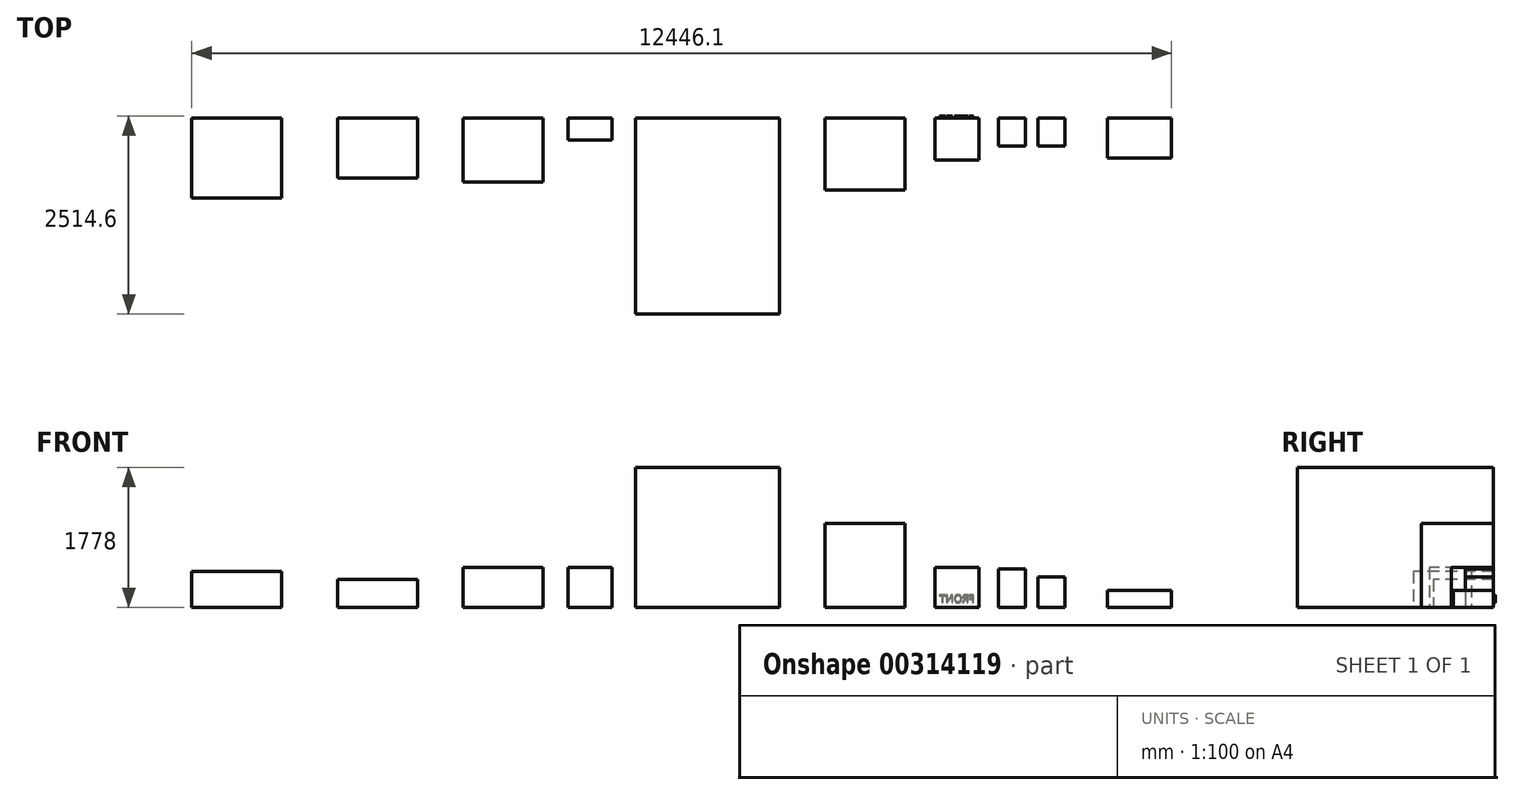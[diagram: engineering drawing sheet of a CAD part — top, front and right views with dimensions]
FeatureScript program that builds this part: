
annotation { "Feature Type Name" : "Feature", "Feature Type Description" : "" }
export const myFeature = defineFeature(function(context is Context, id is Id, definition is map)
    precondition{}
    {
        {
            var Q0;
            Q0=qCreatedBy(makeId("Top.planeOp"),FACE);
            var sketch = newSketch(context, id + "F0", { "sketchPlane" : qUnion([Q0])});
            skLineSegment(sketch, "E0.bottom", {"start": v(-6803, -5124.32) * mm, "end": v(-5660, -5124.32) * mm});
            skLineSegment(sketch, "E0.top", {"start": v(-6803, -6140.32) * mm, "end": v(-5660, -6140.32) * mm});
            skLineSegment(sketch, "E0.left", {"start": v(-6803, -5124.32) * mm, "end": v(-6803, -6140.32) * mm});
            skLineSegment(sketch, "E0.right", {"start": v(-5660, -5124.32) * mm, "end": v(-5660, -6140.32) * mm});
            skLineSegment(sketch, "E1.bottom", {"start": v(-4953.17, -5124.32) * mm, "end": v(-3937.17, -5124.32) * mm});
            skLineSegment(sketch, "E1.top", {"start": v(-4953.17, -5886.32) * mm, "end": v(-3937.17, -5886.32) * mm});
            skLineSegment(sketch, "E1.left", {"start": v(-4953.17, -5124.32) * mm, "end": v(-4953.17, -5886.32) * mm});
            skLineSegment(sketch, "E1.right", {"start": v(-3937.17, -5124.32) * mm, "end": v(-3937.17, -5886.32) * mm});
            skLineSegment(sketch, "E2.bottom", {"start": v(-3360.62, -5124.32) * mm, "end": v(-2344.62, -5124.32) * mm});
            skLineSegment(sketch, "E2.top", {"start": v(-3360.62, -5937.12) * mm, "end": v(-2344.62, -5937.12) * mm});
            skLineSegment(sketch, "E2.left", {"start": v(-3360.62, -5124.32) * mm, "end": v(-3360.62, -5937.12) * mm});
            skLineSegment(sketch, "E2.right", {"start": v(-2344.62, -5124.32) * mm, "end": v(-2344.62, -5937.12) * mm});
            skLineSegment(sketch, "E3.bottom", {"start": v(-2023.28, -5124.32) * mm, "end": v(-1464.48, -5124.32) * mm});
            skLineSegment(sketch, "E3.top", {"start": v(-2023.28, -5403.72) * mm, "end": v(-1464.48, -5403.72) * mm});
            skLineSegment(sketch, "E3.left", {"start": v(-2023.28, -5124.32) * mm, "end": v(-2023.28, -5403.72) * mm});
            skLineSegment(sketch, "E3.right", {"start": v(-1464.48, -5124.32) * mm, "end": v(-1464.48, -5403.72) * mm});
            skLineSegment(sketch, "E4.bottom", {"start": v(-1164.65, -5124.32) * mm, "end": v(664.15, -5124.32) * mm});
            skLineSegment(sketch, "E4.top", {"start": v(-1164.65, -7613.52) * mm, "end": v(664.15, -7613.52) * mm});
            skLineSegment(sketch, "E4.left", {"start": v(-1164.65, -5124.32) * mm, "end": v(-1164.65, -7613.52) * mm});
            skLineSegment(sketch, "E4.right", {"start": v(664.15, -5124.32) * mm, "end": v(664.15, -7613.52) * mm});
            skLineSegment(sketch, "E5.bottom", {"start": v(1237.75, -5124.32) * mm, "end": v(2253.75, -5124.32) * mm});
            skLineSegment(sketch, "E5.top", {"start": v(1237.75, -6038.72) * mm, "end": v(2253.75, -6038.72) * mm});
            skLineSegment(sketch, "E5.left", {"start": v(1237.75, -5124.32) * mm, "end": v(1237.75, -6038.72) * mm});
            skLineSegment(sketch, "E5.right", {"start": v(2253.75, -5124.32) * mm, "end": v(2253.75, -6038.72) * mm});
            skLineSegment(sketch, "E6.bottom", {"start": v(2634.27, -5124.32) * mm, "end": v(3193.07, -5124.32) * mm});
            skLineSegment(sketch, "E6.top", {"start": v(2634.27, -5657.72) * mm, "end": v(3193.07, -5657.72) * mm});
            skLineSegment(sketch, "E6.left", {"start": v(2634.27, -5124.32) * mm, "end": v(2634.27, -5657.72) * mm});
            skLineSegment(sketch, "E6.right", {"start": v(3193.07, -5124.32) * mm, "end": v(3193.07, -5657.72) * mm});
            skLineSegment(sketch, "E7", {"start": v(-7890.9, -5124.32) * mm, "end": v(5758.4, -5124.32) * mm, "construction": true});
            skLineSegment(sketch, "E8.bottom", {"start": v(3441.6, -5124.32) * mm, "end": v(3784.5, -5124.32) * mm});
            skLineSegment(sketch, "E8.top", {"start": v(3441.6, -5479.92) * mm, "end": v(3784.5, -5479.92) * mm});
            skLineSegment(sketch, "E8.left", {"start": v(3441.6, -5124.32) * mm, "end": v(3441.6, -5479.92) * mm});
            skLineSegment(sketch, "E8.right", {"start": v(3784.5, -5124.32) * mm, "end": v(3784.5, -5479.92) * mm});
            skLineSegment(sketch, "E9.bottom", {"start": v(3941.63, -5124.32) * mm, "end": v(4284.53, -5124.32) * mm});
            skLineSegment(sketch, "E9.top", {"start": v(3941.63, -5479.92) * mm, "end": v(4284.53, -5479.92) * mm});
            skLineSegment(sketch, "E9.left", {"start": v(3941.63, -5124.32) * mm, "end": v(3941.63, -5479.92) * mm});
            skLineSegment(sketch, "E9.right", {"start": v(4284.53, -5124.32) * mm, "end": v(4284.53, -5479.92) * mm});
            skLineSegment(sketch, "E10.bottom", {"start": v(4830.3, -5124.32) * mm, "end": v(5643.1, -5124.32) * mm});
            skLineSegment(sketch, "E10.top", {"start": v(4830.3, -5632.32) * mm, "end": v(5643.1, -5632.32) * mm});
            skLineSegment(sketch, "E10.left", {"start": v(4830.3, -5124.32) * mm, "end": v(4830.3, -5632.32) * mm});
            skLineSegment(sketch, "E10.right", {"start": v(5643.1, -5124.32) * mm, "end": v(5643.1, -5632.32) * mm});
            skSolve(sketch);
        }
        {
            var Q0;
            Q0=makeQuery(id+"F0.imprint","IMPRINT",FACE,{"disambiguationData":[TD([[makeQuery(id+"F0.imprint","IMPRINT",EDGE,{"derivedFrom":sQuery(id+"F0.wireOp",EDGE,"E0.bottom")}),-1.0]])]});
            extrude(context, id + "F1", {"entities" : qUnion([Q0]), "depth" : 457.2 * mm});
        }
        {
            var Q0;
            Q0=makeQuery(id+"F0.imprint","IMPRINT",FACE,{"disambiguationData":[TD([[makeQuery(id+"F0.imprint","IMPRINT",EDGE,{"derivedFrom":sQuery(id+"F0.wireOp",EDGE,"E1.bottom")}),-1.0]])]});
            extrude(context, id + "F2", {"entities" : qUnion([Q0]), "depth" : 355.6 * mm});
        }
        {
            var Q0;
            Q0=makeQuery(id+"F0.imprint","IMPRINT",FACE,{"disambiguationData":[TD([[makeQuery(id+"F0.imprint","IMPRINT",EDGE,{"derivedFrom":sQuery(id+"F0.wireOp",EDGE,"E2.bottom")}),-1.0]])]});
            extrude(context, id + "F3", {"entities" : qUnion([Q0]), "depth" : 508 * mm});
        }
        {
            var Q0;
            Q0=makeQuery(id+"F0.imprint","IMPRINT",FACE,{"disambiguationData":[TD([[makeQuery(id+"F0.imprint","IMPRINT",EDGE,{"derivedFrom":sQuery(id+"F0.wireOp",EDGE,"E3.bottom")}),-1.0]])]});
            extrude(context, id + "F4", {"entities" : qUnion([Q0]), "depth" : 508 * mm});
        }
        {
            var Q0;
            Q0=makeQuery(id+"F0.imprint","IMPRINT",FACE,{"disambiguationData":[TD([[makeQuery(id+"F0.imprint","IMPRINT",EDGE,{"derivedFrom":sQuery(id+"F0.wireOp",EDGE,"E4.bottom")}),-1.0]])]});
            extrude(context, id + "F5", {"entities" : qUnion([Q0]), "depth" : 1778 * mm});
        }
        {
            var Q0;
            Q0=makeQuery(id+"F0.imprint","IMPRINT",FACE,{"disambiguationData":[TD([[makeQuery(id+"F0.imprint","IMPRINT",EDGE,{"derivedFrom":sQuery(id+"F0.wireOp",EDGE,"E5.bottom")}),-1.0]])]});
            extrude(context, id + "F6", {"entities" : qUnion([Q0]), "depth" : 1066.8 * mm});
        }
        {
            var Q0;
            Q0=makeQuery(id+"F0.imprint","IMPRINT",FACE,{"disambiguationData":[TD([[makeQuery(id+"F0.imprint","IMPRINT",EDGE,{"derivedFrom":sQuery(id+"F0.wireOp",EDGE,"E6.bottom")}),-1.0]])]});
            extrude(context, id + "F7", {"entities" : qUnion([Q0]), "depth" : 508 * mm});
        }
        {
            var Q0;
            Q0=makeQuery(id+"F0.imprint","IMPRINT",FACE,{"disambiguationData":[TD([[makeQuery(id+"F0.imprint","IMPRINT",EDGE,{"derivedFrom":sQuery(id+"F0.wireOp",EDGE,"E8.bottom")}),-1.0]])]});
            extrude(context, id + "F8", {"entities" : qUnion([Q0]), "depth" : 487.68 * mm});
        }
        {
            var Q0;
            Q0=makeQuery(id+"F0.imprint","IMPRINT",FACE,{"disambiguationData":[TD([[makeQuery(id+"F0.imprint","IMPRINT",EDGE,{"derivedFrom":sQuery(id+"F0.wireOp",EDGE,"E9.bottom")}),-1.0]])]});
            extrude(context, id + "F9", {"entities" : qUnion([Q0]), "depth" : 388.62 * mm});
        }
        {
            var Q0;
            Q0=makeQuery(id+"F0.imprint","IMPRINT",FACE,{"disambiguationData":[TD([[makeQuery(id+"F0.imprint","IMPRINT",EDGE,{"derivedFrom":sQuery(id+"F0.wireOp",EDGE,"E10.bottom")}),-1.0]])]});
            extrude(context, id + "F10", {"entities" : qUnion([Q0]), "depth" : 215.9 * mm});
        }
        {
            var Q0;
            Q0=makeQuery(id+"F7.opExtrude","SWEPT_FACE",FACE,{"disambiguationData":[OSD([sQuery(id+"F0.wireOp",EDGE,"E6.bottom")])]});
            var sketch = newSketch(context, id + "F11", { "sketchPlane" : qUnion([Q0])});
            skText(sketch, "E11", { "text": "FRONT", "fontName": "OpenSans-Regular.ttf"});
            const initialGuessF11  = {"E11": [-3.13883, 0.06103, 1, 0, 0.09925]};
            skSetInitialGuess(sketch, initialGuessF11);
            skSolve(sketch);
        }
        {
            var Q0;
            Q0 = qSketchRegion(id + "F11", true);
            extrude(context, id + "F12", {"entities" : qUnion([Q0]), "operationType" : NewBodyOperationType.ADD, "depth" : 25.4 * mm});
        }
    });
